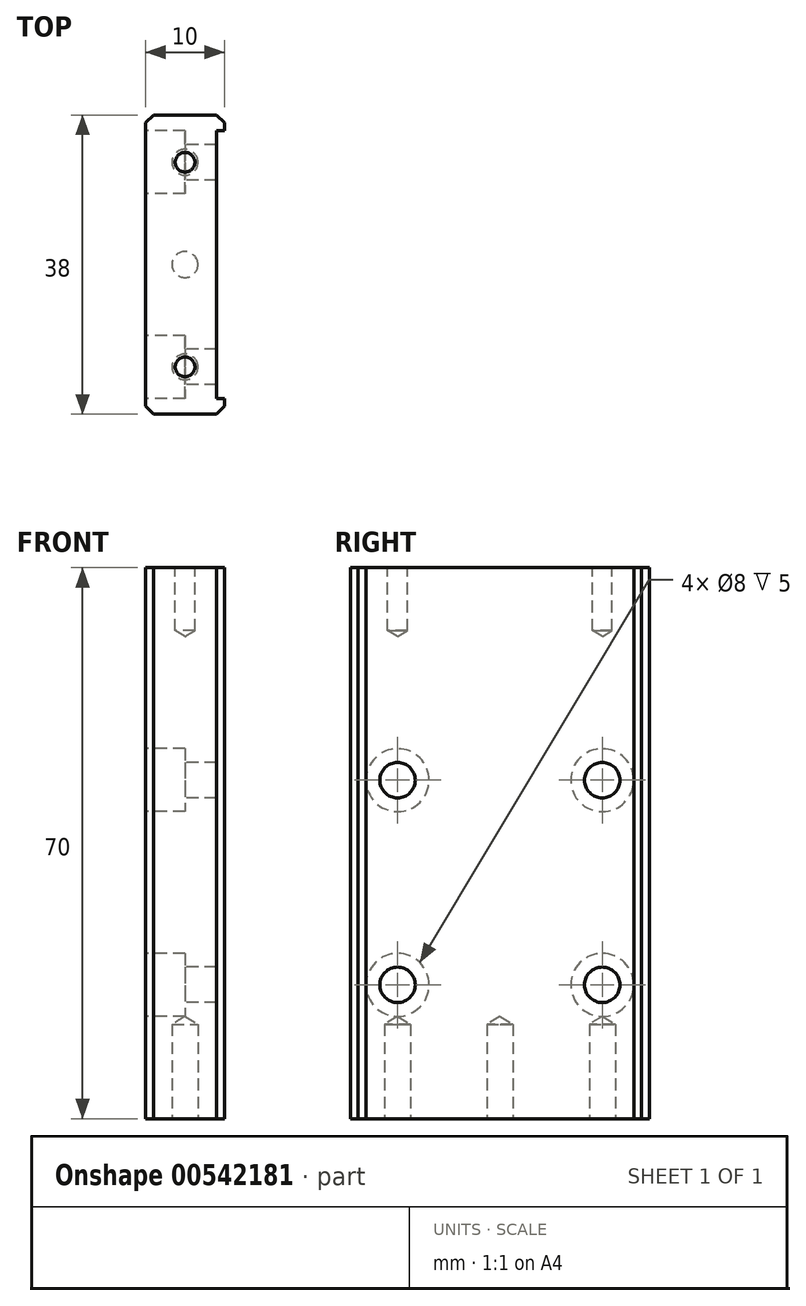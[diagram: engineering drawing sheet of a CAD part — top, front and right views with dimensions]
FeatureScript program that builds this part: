
annotation { "Feature Type Name" : "Feature", "Feature Type Description" : "" }
export const myFeature = defineFeature(function(context is Context, id is Id, definition is map)
    precondition{}
    {
        {
            var Q0;
            Q0=qCreatedBy(makeId("Top.planeOp"),FACE);
            var sketch = newSketch(context, id + "F0", { "sketchPlane" : qUnion([Q0])});
            skLineSegment(sketch, "E0", {"start": v(5, 17) * mm, "end": v(5, 19) * mm});
            skLineSegment(sketch, "E1", {"start": v(5, 19) * mm, "end": v(-5, 19) * mm});
            skLineSegment(sketch, "E2", {"start": v(-5, 19) * mm, "end": v(-5, -19) * mm});
            skLineSegment(sketch, "E3", {"start": v(-5, -19) * mm, "end": v(5, -19) * mm});
            skLineSegment(sketch, "E4", {"start": v(5, -19) * mm, "end": v(5, -17) * mm});
            skLineSegment(sketch, "E5", {"start": v(4, 0) * mm, "end": v(4, -17) * mm});
            skLineSegment(sketch, "E6", {"start": v(4, -17) * mm, "end": v(5, -17) * mm});
            skLineSegment(sketch, "E7", {"start": v(4, 0) * mm, "end": v(4, 17) * mm});
            skLineSegment(sketch, "E8", {"start": v(4, 17) * mm, "end": v(5, 17) * mm});
            skSolve(sketch);
        }
        {
            var Q0;
            Q0=makeQuery(id+"F0.imprint","IMPRINT",FACE,{"disambiguationData":[TD([[makeQuery(id+"F0.imprint","IMPRINT",EDGE,{"derivedFrom":sQuery(id+"F0.wireOp",EDGE,"E0")}),1.0]])]});
            extrude(context, id + "F1", {"entities" : qUnion([Q0]), "endBound" : BoundingType.SYMMETRIC, "depth" : 70 * mm, "offsetDistance" : 25 * mm});
        }
        {
            var Q0;
            Q0=makeQuery(id+"F1.opExtrude","SWEPT_EDGE",EDGE,{"disambiguationData":[OSD([sQuery(id+"F0.wireOp",EDGE,"E1"),sQuery(id+"F0.wireOp",EDGE,"E2")])]});
            var Q1;
            Q1=makeQuery(id+"F1.opExtrude","SWEPT_EDGE",EDGE,{"disambiguationData":[OSD([sQuery(id+"F0.wireOp",EDGE,"E0"),sQuery(id+"F0.wireOp",EDGE,"E1")])]});
            var Q2;
            Q2=makeQuery(id+"F1.opExtrude","SWEPT_EDGE",EDGE,{"disambiguationData":[OSD([sQuery(id+"F0.wireOp",EDGE,"E2"),sQuery(id+"F0.wireOp",EDGE,"E3")])]});
            var Q3;
            Q3=makeQuery(id+"F1.opExtrude","SWEPT_EDGE",EDGE,{"disambiguationData":[OSD([sQuery(id+"F0.wireOp",EDGE,"E3"),sQuery(id+"F0.wireOp",EDGE,"E4")])]});
            chamfer(context, id + "F2", {"entities" : qUnion([Q0, Q1, Q2, Q3]), "width" : 1 * mm, "tangentPropagation" : true});
        }
        {
            var Q0;
            Q0=makeQuery(id+"F1.opExtrude","CAP_FACE",FACE,{"disambiguationData":[OSD([sQuery(id+"F0.wireOp",EDGE,"E0"),sQuery(id+"F0.wireOp",EDGE,"E1"),sQuery(id+"F0.wireOp",EDGE,"E2"),sQuery(id+"F0.wireOp",EDGE,"E3"),sQuery(id+"F0.wireOp",EDGE,"E4"),sQuery(id+"F0.wireOp",EDGE,"E5"),sQuery(id+"F0.wireOp",EDGE,"E6"),sQuery(id+"F0.wireOp",EDGE,"E7"),sQuery(id+"F0.wireOp",EDGE,"E8")])],"isStart":false});
            var sketch = newSketch(context, id + "F3", { "sketchPlane" : qUnion([Q0])});
            skLineSegment(sketch, "E9", {"start": v(0, 0) * mm, "end": v(0, 13) * mm});
            skLineSegment(sketch, "E10", {"start": v(0, 0) * mm, "end": v(0, -13) * mm});
            skSolve(sketch);
        }
        {
            var Q0;
            Q0=sQuery(id+"F3.wireOp",VERTEX,"E9.end");
            var Q1;
            Q1=sQuery(id+"F3.wireOp",VERTEX,"E10.end");
            var Q2;
            Q2=makeQuery(id+"F1.opExtrude","SWEPT_BODY",BODY,{"disambiguationData":[OSD([sQuery(id+"F0.wireOp",EDGE,"E0"),sQuery(id+"F0.wireOp",EDGE,"E1"),sQuery(id+"F0.wireOp",EDGE,"E2"),sQuery(id+"F0.wireOp",EDGE,"E3"),sQuery(id+"F0.wireOp",EDGE,"E4"),sQuery(id+"F0.wireOp",EDGE,"E5"),sQuery(id+"F0.wireOp",EDGE,"E6"),sQuery(id+"F0.wireOp",EDGE,"E7"),sQuery(id+"F0.wireOp",EDGE,"E8")])]});
            hole(context, id + "F4", {"style" : HoleStyle.SIMPLE, "endStyle" : HoleEndStyle.BLIND, "standardTappedOrClearance" : lookupTablePath({ "standard" : "ISO", "engagement" : "75%", "pitch" : "0.5 mm", "size" : "M3", "type" : "Tapped" }), "standardBlindInLast" : lookupTablePath({ "standard" : "ISO", "engagement" : "75%", "pitch" : "0.5 mm", "size" : "M3", "type" : "Tapped" }), "holeDiameter" : 2.5 * mm, "showTappedDepth" : true, "holeDepth" : 8 * mm, "isTappedThrough" : true, "tappedDepth" : 6.5 * mm, "tapClearance" : 3, "startFromSketch" : true, "locations" : qUnion([Q0, Q1]), "scope" : qUnion([Q2]), "majorDiameter" : 3 * mm});
        }
        {
            var Q0;
            Q0=makeQuery(id+"F1.opExtrude","SWEPT_FACE",FACE,{"disambiguationData":[OSD([sQuery(id+"F0.wireOp",EDGE,"E2")])]});
            var sketch = newSketch(context, id + "F5", { "sketchPlane" : qUnion([Q0])});
            skPoint(sketch, "E11.endSnap0", {"position": v(0, -35) * mm});
            skLineSegment(sketch, "E12", {"start": v(-13, -18) * mm, "end": v(-13, 8) * mm});
            skLineSegment(sketch, "E13", {"start": v(13, -18) * mm, "end": v(13, 8) * mm});
            skSolve(sketch);
        }
        {
            var Q0;
            Q0=sQuery(id+"F5.wireOp",VERTEX,"E12.end");
            var Q1;
            Q1=sQuery(id+"F5.wireOp",VERTEX,"E13.end");
            var Q2;
            Q2=sQuery(id+"F5.wireOp",VERTEX,"E13.start");
            var Q3;
            Q3=sQuery(id+"F5.wireOp",VERTEX,"E12.start");
            var Q4;
            Q4=makeQuery(id+"F1.opExtrude","SWEPT_BODY",BODY,{"disambiguationData":[OSD([sQuery(id+"F0.wireOp",EDGE,"E0"),sQuery(id+"F0.wireOp",EDGE,"E1"),sQuery(id+"F0.wireOp",EDGE,"E2"),sQuery(id+"F0.wireOp",EDGE,"E3"),sQuery(id+"F0.wireOp",EDGE,"E4"),sQuery(id+"F0.wireOp",EDGE,"E5"),sQuery(id+"F0.wireOp",EDGE,"E6"),sQuery(id+"F0.wireOp",EDGE,"E7"),sQuery(id+"F0.wireOp",EDGE,"E8")])]});
            hole(context, id + "F6", {"style" : HoleStyle.C_BORE, "endStyle" : HoleEndStyle.THROUGH, "holeDiameter" : 4.5 * mm, "cBoreDiameter" : 8 * mm, "cBoreDepth" : 5 * mm, "isTappedThrough" : true, "tappedDepth" : 6.5 * mm, "tapClearance" : 3, "startFromSketch" : true, "locations" : qUnion([Q0, Q1, Q2, Q3]), "scope" : qUnion([Q4])});
        }
        {
            var Q0;
            Q0=makeQuery(id+"F1.opExtrude","CAP_FACE",FACE,{"disambiguationData":[OSD([sQuery(id+"F0.wireOp",EDGE,"E0"),sQuery(id+"F0.wireOp",EDGE,"E1"),sQuery(id+"F0.wireOp",EDGE,"E2"),sQuery(id+"F0.wireOp",EDGE,"E3"),sQuery(id+"F0.wireOp",EDGE,"E4"),sQuery(id+"F0.wireOp",EDGE,"E5"),sQuery(id+"F0.wireOp",EDGE,"E6"),sQuery(id+"F0.wireOp",EDGE,"E7"),sQuery(id+"F0.wireOp",EDGE,"E8")])],"isStart":true});
            var sketch = newSketch(context, id + "F7", { "sketchPlane" : qUnion([Q0])});
            skLineSegment(sketch, "E14", {"start": v(0, 0) * mm, "end": v(0, 13) * mm});
            skLineSegment(sketch, "E15", {"start": v(0, 0) * mm, "end": v(0, -13) * mm});
            skSolve(sketch);
        }
        {
            var Q0;
            Q0=sQuery(id+"F7.wireOp",VERTEX,"E14.end");
            var Q1;
            Q1=sQuery(id+"F7.wireOp",VERTEX,"E15.start");
            var Q2;
            Q2=sQuery(id+"F7.wireOp",VERTEX,"E15.end");
            var Q3;
            Q3=makeQuery(id+"F1.opExtrude","SWEPT_BODY",BODY,{"disambiguationData":[OSD([sQuery(id+"F0.wireOp",EDGE,"E0"),sQuery(id+"F0.wireOp",EDGE,"E1"),sQuery(id+"F0.wireOp",EDGE,"E2"),sQuery(id+"F0.wireOp",EDGE,"E3"),sQuery(id+"F0.wireOp",EDGE,"E4"),sQuery(id+"F0.wireOp",EDGE,"E5"),sQuery(id+"F0.wireOp",EDGE,"E6"),sQuery(id+"F0.wireOp",EDGE,"E7"),sQuery(id+"F0.wireOp",EDGE,"E8")])]});
            hole(context, id + "F8", {"style" : HoleStyle.SIMPLE, "endStyle" : HoleEndStyle.BLIND, "standardTappedOrClearance" : lookupTablePath({ "standard" : "ISO", "engagement" : "75%", "pitch" : "0.7 mm", "size" : "M4", "type" : "Tapped" }), "standardBlindInLast" : lookupTablePath({ "standard" : "ISO", "engagement" : "75%", "pitch" : "0.7 mm", "size" : "M4", "type" : "Tapped" }), "holeDiameter" : 3.3 * mm, "showTappedDepth" : true, "holeDepth" : 12 * mm, "isTappedThrough" : true, "tappedDepth" : 9.9 * mm, "tapClearance" : 3, "startFromSketch" : true, "locations" : qUnion([Q0, Q1, Q2]), "scope" : qUnion([Q3]), "majorDiameter" : 4 * mm});
        }
    });
